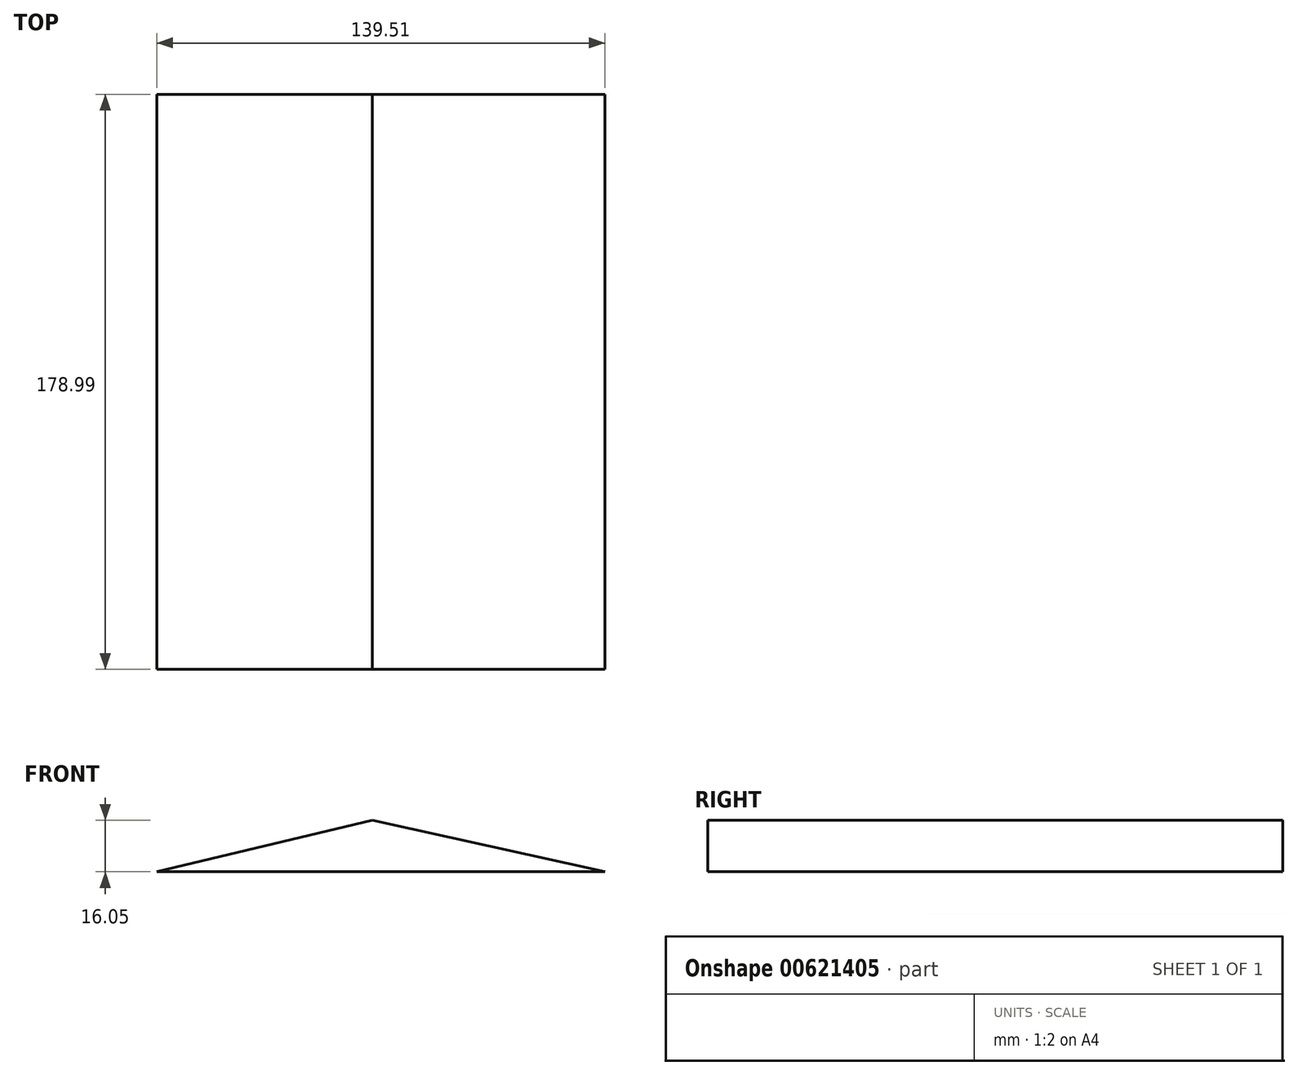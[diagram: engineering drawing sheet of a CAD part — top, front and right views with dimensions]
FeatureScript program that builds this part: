
annotation { "Feature Type Name" : "Feature", "Feature Type Description" : "" }
export const myFeature = defineFeature(function(context is Context, id is Id, definition is map)
    precondition{}
    {
        {
            var Q0;
            Q0=qCreatedBy(makeId("Front.planeOp"),FACE);
            var sketch = newSketch(context, id + "F0", { "sketchPlane" : qUnion([Q0])});
            skLineSegment(sketch, "E0", {"start": v(-67.18, -16.05) * mm, "end": v(72.33, -16.05) * mm});
            skLineSegment(sketch, "E1", {"start": v(72.33, -16.05) * mm, "end": v(0, 0) * mm});
            skLineSegment(sketch, "E2", {"start": v(0, 0) * mm, "end": v(-67.18, -16.05) * mm});
            skSolve(sketch);
        }
        {
            var Q0;
            Q0 = qSketchRegion(id + "F0", true);
            extrude(context, id + "F1", {"entities" : qUnion([Q0]), "depth" : 179 * mm, "offsetDistance" : 25.4 * mm});
        }
    });
